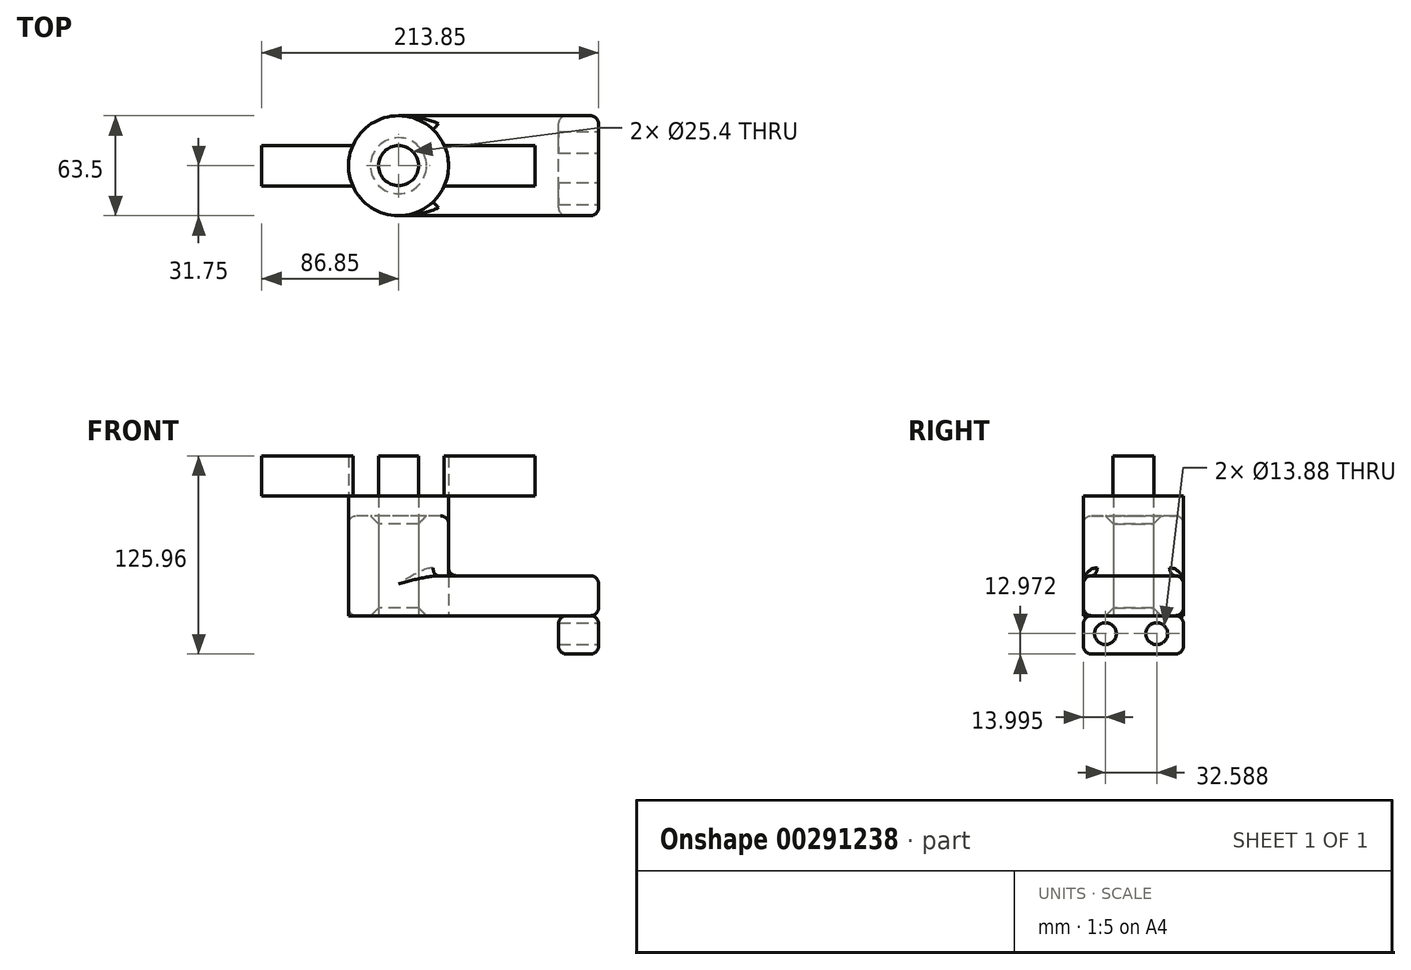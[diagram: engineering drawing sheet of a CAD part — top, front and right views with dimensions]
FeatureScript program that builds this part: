
annotation { "Feature Type Name" : "Feature", "Feature Type Description" : "" }
export const myFeature = defineFeature(function(context is Context, id is Id, definition is map)
    precondition{}
    {
        {
            var Q0;
            Q0=qCreatedBy(makeId("Top.planeOp"),FACE);
            var sketch = newSketch(context, id + "F0", { "sketchPlane" : qUnion([Q0])});
            skLineSegment(sketch, "E0.bottom", {"start": v(0, 0) * mm, "end": v(127, 0) * mm});
            skLineSegment(sketch, "E0.top", {"start": v(0, 63.5) * mm, "end": v(127, 63.5) * mm});
            skLineSegment(sketch, "E0.left", {"start": v(0, 0) * mm, "end": v(0, 63.5) * mm});
            skLineSegment(sketch, "E0.right", {"start": v(127, 0) * mm, "end": v(127, 63.5) * mm});
            skCircle(sketch, "E1", {"center": v(0, 31.75) * mm, "radius": 31.75 * mm});
            skCircle(sketch, "E2", {"center": v(0, 31.75) * mm, "radius": 12.7 * mm});
            skSolve(sketch);
        }
        {
            var Q0;
            {var subQ1=sQuery(id+"F0.wireOp",EDGE,"E0.left");var subQ3=sQuery(id+"F0.wireOp",EDGE,"E2");var subQ4=makeQuery(id+"F0.imprint","INTERSECT",VERTEX,{"disambiguationData":[OD(0.0)],"derivedFrom":[subQ1,subQ3]});Q0=makeQuery(id+"F0.imprint","IMPRINT",FACE,{"disambiguationData":[TD([[makeQuery(id+"F0.imprint","IMPRINT",EDGE,{"disambiguationData":[TD([[subQ4,1.0]])],"derivedFrom":subQ3}),-1.0]])]});}
            var Q1;
            {var subQ1=sQuery(id+"F0.wireOp",EDGE,"E0.left");var subQ3=sQuery(id+"F0.wireOp",EDGE,"E2");var subQ4=makeQuery(id+"F0.imprint","INTERSECT",VERTEX,{"disambiguationData":[OD(0.0)],"derivedFrom":[subQ1,subQ3]});Q1=makeQuery(id+"F0.imprint","IMPRINT",FACE,{"disambiguationData":[TD([[makeQuery(id+"F0.imprint","IMPRINT",EDGE,{"disambiguationData":[TD([[subQ4,-1.0]])],"derivedFrom":subQ3}),-1.0]])]});}
            var Q2;
            {var subQ0=sQuery(id+"F0.wireOp",EDGE,"E0.bottom");Q2=makeQuery(id+"F0.imprint","IMPRINT",FACE,{"disambiguationData":[TD([[makeQuery(id+"F0.imprint","IMPRINT",EDGE,{"derivedFrom":subQ0}),1.0]])]});}
            extrude(context, id + "F1", {"entities" : qUnion([Q0, Q1, Q2]), "depth" : 25.4 * mm});
        }
        {
            var Q0;
            {var subQ1=sQuery(id+"F0.wireOp",EDGE,"E0.left");var subQ3=sQuery(id+"F0.wireOp",EDGE,"E2");var subQ4=makeQuery(id+"F0.imprint","INTERSECT",VERTEX,{"disambiguationData":[OD(0.0)],"derivedFrom":[subQ1,subQ3]});Q0=makeQuery(id+"F0.imprint","IMPRINT",FACE,{"disambiguationData":[TD([[makeQuery(id+"F0.imprint","IMPRINT",EDGE,{"disambiguationData":[TD([[subQ4,1.0]])],"derivedFrom":subQ3}),-1.0]])]});}
            var Q1;
            {var subQ1=sQuery(id+"F0.wireOp",EDGE,"E0.left");var subQ3=sQuery(id+"F0.wireOp",EDGE,"E2");var subQ4=makeQuery(id+"F0.imprint","INTERSECT",VERTEX,{"disambiguationData":[OD(0.0)],"derivedFrom":[subQ1,subQ3]});Q1=makeQuery(id+"F0.imprint","IMPRINT",FACE,{"disambiguationData":[TD([[makeQuery(id+"F0.imprint","IMPRINT",EDGE,{"disambiguationData":[TD([[subQ4,-1.0]])],"derivedFrom":subQ3}),-1.0]])]});}
            extrude(context, id + "F2", {"entities" : qUnion([Q0, Q1]), "operationType" : NewBodyOperationType.ADD, "depth" : 63.5 * mm});
        }
        {
            var Q0;
            Q0=makeQuery(id+"F1.opExtrude","SWEPT_FACE",FACE,{"disambiguationData":[OSD([sQuery(id+"F0.wireOp",EDGE,"E0.right")])]});
            var sketch = newSketch(context, id + "F3", { "sketchPlane" : qUnion([Q0])});
            skLineSegment(sketch, "E3.bottom", {"start": v(0, 25.4) * mm, "end": v(63.5, 25.4) * mm});
            skLineSegment(sketch, "E3.top", {"start": v(0, -24.36) * mm, "end": v(63.5, -24.36) * mm});
            skLineSegment(sketch, "E3.left", {"start": v(0, 25.4) * mm, "end": v(0, -24.36) * mm});
            skLineSegment(sketch, "E3.right", {"start": v(63.5, 25.4) * mm, "end": v(63.5, -24.36) * mm});
            skSolve(sketch);
        }
        {
            var Q0;
            {var subQ0=sQuery(id+"F3.wireOp",EDGE,"E3.top");Q0=makeQuery(id+"F3.imprint","IMPRINT",FACE,{"disambiguationData":[TD([[makeQuery(id+"F3.imprint","IMPRINT",EDGE,{"derivedFrom":subQ0}),1.0]])]});}
            var sketch = newSketch(context, id + "F4", { "sketchPlane" : qUnion([Q0])});
            skLineSegment(sketch, "E4", {"start": v(30.29, 0) * mm, "end": v(30.29, -24.42) * mm, "construction": true});
            skCircle(sketch, "E5", {"center": v(14, -11.39) * mm, "radius": 6.94 * mm});
            skCircle(sketch, "E6.MirrorC", {"center": v(46.58, -11.39) * mm, "radius": 6.94 * mm});
            skSolve(sketch);
        }
        {
            var Q0;
            Q0=makeQuery(id+"F4.imprint","IMPRINT",FACE,{"disambiguationData":[TD([[makeQuery(id+"F4.imprint","IMPRINT",EDGE,{"derivedFrom":sQuery(id+"F4.wireOp",EDGE,"E5")}),-1.0]])]});
            extrude(context, id + "F5", {"entities" : qUnion([Q0]), "oppositeDirection" : true, "depth" : 25.4 * mm});
        }
        {
            var Q0;
            Q0=makeQuery(id+"F1.opExtrude","CAP_EDGE",EDGE,{"disambiguationData":[OSD([sQuery(id+"F0.wireOp",EDGE,"E0.bottom")])],"isStart":false});
            var Q1;
            Q1=makeQuery(id+"F1.opExtrude","CAP_EDGE",EDGE,{"disambiguationData":[OSD([sQuery(id+"F0.wireOp",EDGE,"E0.right")])],"isStart":false});
            var Q2;
            Q2=makeQuery(id+"F1.opExtrude","CAP_EDGE",EDGE,{"disambiguationData":[OSD([sQuery(id+"F0.wireOp",EDGE,"E0.top")])],"isStart":false});
            var Q3;
            Q3=makeQuery(id+"F1.opExtrude","SWEPT_EDGE",EDGE,{"disambiguationData":[OSD([sQuery(id+"F0.wireOp",EDGE,"E0.bottom"),sQuery(id+"F0.wireOp",EDGE,"E0.right")])]});
            var Q4;
            Q4=makeQuery(id+"F1.opExtrude","SWEPT_EDGE",EDGE,{"disambiguationData":[OSD([sQuery(id+"F0.wireOp",EDGE,"E0.top"),sQuery(id+"F0.wireOp",EDGE,"E0.right")])]});
            var Q5;
            Q5=makeQuery(id+"F5.opExtrude","CAP_EDGE",EDGE,{"disambiguationData":[OSD([sQuery(id+"F3.wireOp",EDGE,"E3.left")])],"isStart":true});
            var Q6;
            Q6=makeQuery(id+"F5.opExtrude","CAP_EDGE",EDGE,{"disambiguationData":[OSD([sQuery(id+"F3.wireOp",EDGE,"E3.right")])],"isStart":true});
            var Q7;
            Q7=makeQuery(id+"F5.opExtrude","CAP_EDGE",EDGE,{"disambiguationData":[OSD([sQuery(id+"F3.wireOp",EDGE,"E3.top")])],"isStart":true});
            var Q8;
            Q8=makeQuery(id+"F5.opExtrude","SWEPT_EDGE",EDGE,{"disambiguationData":[OSD([sQuery(id+"F3.wireOp",EDGE,"E3.top"),sQuery(id+"F3.wireOp",EDGE,"E3.left")])]});
            var Q9;
            Q9=makeQuery(id+"F5.opExtrude","CAP_EDGE",EDGE,{"disambiguationData":[OSD([sQuery(id+"F3.wireOp",EDGE,"E3.left")])],"isStart":false});
            var Q10;
            Q10=makeQuery(id+"F5.opExtrude","CAP_EDGE",EDGE,{"disambiguationData":[OSD([sQuery(id+"F3.wireOp",EDGE,"E3.top")])],"isStart":false});
            var Q11;
            Q11=makeQuery(id+"F5.opExtrude","SWEPT_EDGE",EDGE,{"disambiguationData":[OSD([sQuery(id+"F3.wireOp",EDGE,"E3.top"),sQuery(id+"F3.wireOp",EDGE,"E3.right")])]});
            var Q12;
            Q12=makeQuery(id+"F5.opExtrude","CAP_EDGE",EDGE,{"disambiguationData":[OSD([sQuery(id+"F3.wireOp",EDGE,"E3.right")])],"isStart":false});
            var Q13;
            Q13=makeQuery(id+"F2.opExtrude","CAP_EDGE",EDGE,{"disambiguationData":[OSD([sQuery(id+"F0.wireOp",EDGE,"E1")])],"isStart":false});
            fillet(context, id + "F6", {"entities" : qUnion([Q0, Q1, Q2, Q3, Q4, Q5, Q6, Q7, Q8, Q9, Q10, Q11, Q12, Q13]), "radius" : 5.08 * mm, "tangentPropagation" : true, "allowEdgeOverflow" : false});
        }
        {
            var Q0;
            {var subQ0=sQuery(id+"F0.wireOp",EDGE,"E2");Q0=makeQuery(id+"F2.boolean.opBoolean","MERGE",FACE,{"derivedFrom":[makeQuery(id+"F1.opExtrude","SWEPT_FACE",FACE,{"disambiguationData":[OSD([subQ0])]}),makeQuery(id+"F2.opExtrude","SWEPT_FACE",FACE,{"disambiguationData":[OSD([subQ0])]})]});}
            chamfer(context, id + "F7", {"entities" : qUnion([Q0]), "width" : 5.08 * mm, "tangentPropagation" : true});
        }
        {
            var Q0;
            Q0=makeQuery(id+"F5.opExtrude","CAP_EDGE",EDGE,{"disambiguationData":[OSD([sQuery(id+"F0.wireOp",EDGE,"E0.right")])],"isStart":false});
            var Q1;
            Q1=makeQuery(id+"F1.opExtrude","CAP_EDGE",EDGE,{"disambiguationData":[OSD([sQuery(id+"F0.wireOp",EDGE,"E1")])],"isStart":true});
            var Q2;
            {var subQ0=sQuery(id+"F0.wireOp",EDGE,"E1");Q2=makeQuery(id+"F2.boolean.opBoolean","INTERSECT",EDGE,{"derivedFrom":[makeQuery(id+"F1.opExtrude","CAP_FACE",FACE,{"disambiguationData":[OSD([sQuery(id+"F0.wireOp",EDGE,"E0.bottom"),sQuery(id+"F0.wireOp",EDGE,"E0.top"),sQuery(id+"F0.wireOp",EDGE,"E0.right"),subQ0,sQuery(id+"F0.wireOp",EDGE,"E2")])],"isStart":false}),makeQuery(id+"F2.opExtrude","SWEPT_FACE",FACE,{"disambiguationData":[OSD([subQ0])]})]});}
            fillet(context, id + "F8", {"entities" : qUnion([Q0, Q1, Q2]), "radius" : 5.08 * mm, "tangentPropagation" : true, "allowEdgeOverflow" : false});
        }
        {
            var Q0;
            {var subQ0=sQuery(id+"F0.wireOp",EDGE,"E2");var subQ1=sQuery(id+"F0.wireOp",EDGE,"E0.left");var subQ2=makeQuery(id+"F0.imprint","INTERSECT",VERTEX,{"disambiguationData":[OD(0.0)],"derivedFrom":[subQ1,subQ0]});Q0=makeQuery(id+"F0.imprint","IMPRINT",FACE,{"disambiguationData":[TD([[makeQuery(id+"F0.imprint","IMPRINT",EDGE,{"disambiguationData":[TD([[subQ2,-1.0]])],"derivedFrom":subQ1}),-1.0]])]});}
            var Q1;
            {var subQ0=sQuery(id+"F0.wireOp",EDGE,"E2");var subQ1=sQuery(id+"F0.wireOp",EDGE,"E0.left");var subQ2=makeQuery(id+"F0.imprint","INTERSECT",VERTEX,{"disambiguationData":[OD(0.0)],"derivedFrom":[subQ1,subQ0]});Q1=makeQuery(id+"F0.imprint","IMPRINT",FACE,{"disambiguationData":[TD([[makeQuery(id+"F0.imprint","IMPRINT",EDGE,{"disambiguationData":[TD([[subQ2,-1.0]])],"derivedFrom":subQ1}),1.0]])]});}
            extrude(context, id + "F9", {"entities" : qUnion([Q0, Q1]), "depth" : 76.2 * mm});
        }
        {
            var Q0;
            Q0=makeQuery(id+"F9.opExtrude","CAP_FACE",FACE,{"disambiguationData":[OSD([sQuery(id+"F0.wireOp",EDGE,"E2")])],"isStart":false});
            var sketch = newSketch(context, id + "F10", { "sketchPlane" : qUnion([Q0])});
            skLineSegment(sketch, "E7.bottom", {"start": v(86.85, 18.83) * mm, "end": v(-86.85, 18.83) * mm});
            skLineSegment(sketch, "E7.top", {"start": v(86.85, 44.67) * mm, "end": v(-86.85, 44.67) * mm});
            skLineSegment(sketch, "E7.left", {"start": v(86.85, 18.83) * mm, "end": v(86.85, 44.67) * mm});
            skLineSegment(sketch, "E7.right", {"start": v(-86.85, 18.83) * mm, "end": v(-86.85, 44.67) * mm});
            skPoint(sketch, "E7.middle", {"position": v(0, 31.75) * mm});
            skSolve(sketch);
        }
        {
            var Q0;
            Q0=makeQuery(id+"F10.imprint","IMPRINT",FACE,{"disambiguationData":[TD([[makeQuery(id+"F10.imprint","IMPRINT",EDGE,{"derivedFrom":sQuery(id+"F10.wireOp",EDGE,"E7.bottom")}),-1.0]])]});
            var Q1;
            Q1=makeQuery(id+"F10.imprint","IMPRINT",FACE,{"disambiguationData":[TD([[makeQuery(id+"F10.imprint","IMPRINT",EDGE,{"derivedFrom":makeQuery(id+"F9.opExtrude","CAP_EDGE",EDGE,{"disambiguationData":[OSD([sQuery(id+"F0.wireOp",EDGE,"E2")])],"isStart":false})}),1.0]])]});
            extrude(context, id + "F11", {"entities" : qUnion([Q0, Q1]), "depth" : 25.4 * mm});
        }
    });
